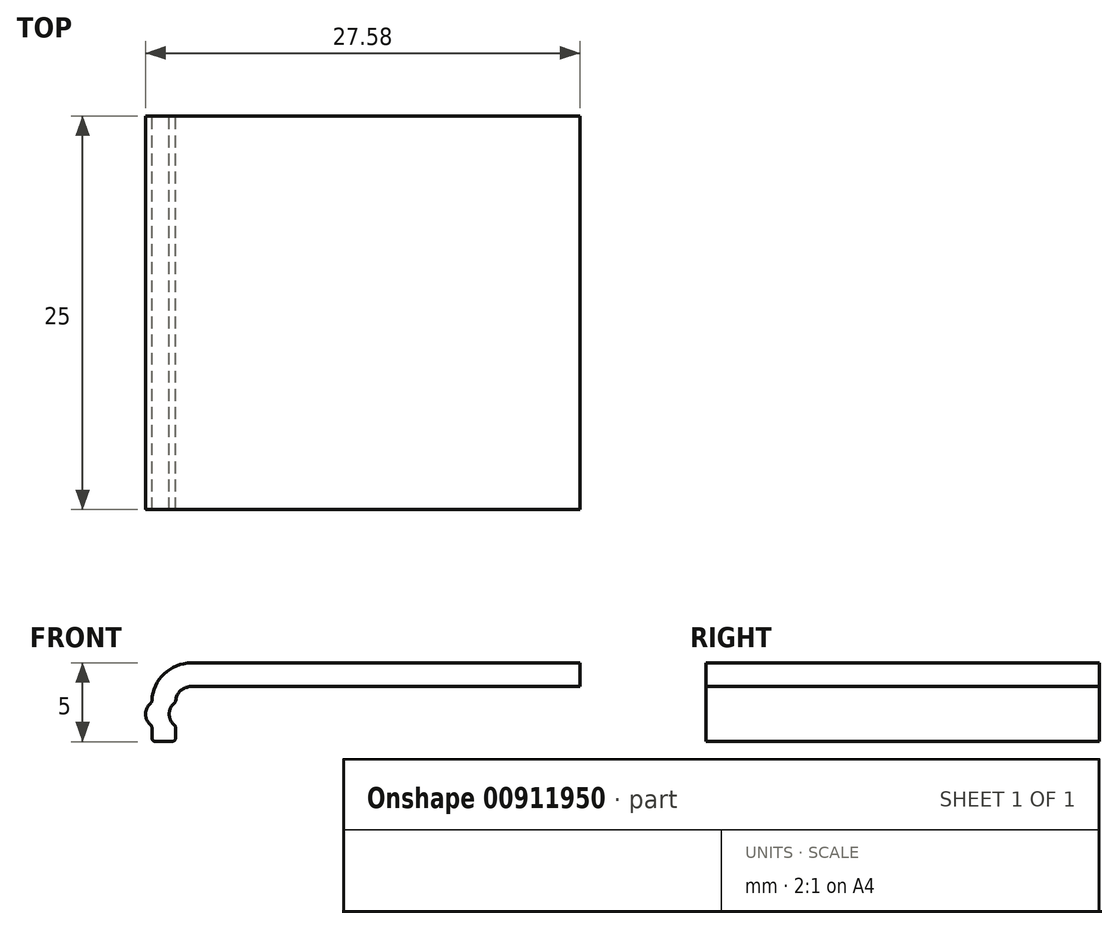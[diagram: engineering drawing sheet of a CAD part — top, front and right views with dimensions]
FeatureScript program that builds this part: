
annotation { "Feature Type Name" : "Feature", "Feature Type Description" : "" }
export const myFeature = defineFeature(function(context is Context, id is Id, definition is map)
    precondition{}
    {
        {
            var Q0;
            Q0=qCreatedBy(makeId("Front.planeOp"),FACE);
            var sketch = newSketch(context, id + "F0", { "sketchPlane" : qUnion([Q0])});
            skLineSegment(sketch, "E0", {"start": v(0, 0) * mm, "end": v(-24.68, 0) * mm});
            skArc(sketch, "E1", {"start": v(-24.68, 0) * mm, "mid": v(-25.4, -0.3) * mm, "end": v(-25.68, -1) * mm});
            skLineSegment(sketch, "E2", {"start": v(-25.68, -1) * mm, "end": v(-25.68, -1) * mm});
            skArc(sketch, "E3", {"start": v(-25.68, -1) * mm, "mid": v(-26.08, -1.75) * mm, "end": v(-25.68, -2.5) * mm});
            skLineSegment(sketch, "E4", {"start": v(-25.68, -2.5) * mm, "end": v(-25.68, -3.5) * mm});
            skLineSegment(sketch, "E5", {"start": v(-27.18, -3.5) * mm, "end": v(-25.68, -3.5) * mm});
            skLineSegment(sketch, "E6", {"start": v(-25.68, -1) * mm, "end": v(-25.68, -2.5) * mm, "construction": true});
            skLineSegment(sketch, "E7", {"start": v(-25.68, -1.75) * mm, "end": v(-26.08, -1.75) * mm, "construction": true});
            skLineSegment(sketch, "E8", {"start": v(-27.18, -3.5) * mm, "end": v(-27.18, -2.5) * mm});
            skArc(sketch, "E9", {"start": v(-27.18, -1) * mm, "mid": v(-27.58, -1.75) * mm, "end": v(-27.18, -2.5) * mm});
            skLineSegment(sketch, "E10", {"start": v(-27.18, -1) * mm, "end": v(-27.18, -1) * mm});
            skLineSegment(sketch, "E11", {"start": v(-27.18, -1) * mm, "end": v(-27.18, -2.5) * mm, "construction": true});
            skLineSegment(sketch, "E12", {"start": v(-27.18, -1.75) * mm, "end": v(-27.58, -1.75) * mm, "construction": true});
            skArc(sketch, "E13", {"start": v(-24.68, 1.5) * mm, "mid": v(-26.45, 0.77) * mm, "end": v(-27.18, -1) * mm});
            skLineSegment(sketch, "E14", {"start": v(-24.68, 1.5) * mm, "end": v(0, 1.5) * mm});
            skLineSegment(sketch, "E15", {"start": v(0, 1.5) * mm, "end": v(0, 0) * mm});
            skSolve(sketch);
        }
        {
            var Q0;
            Q0=makeQuery(id+"F0.imprint","IMPRINT",FACE,{"disambiguationData":[TD([[makeQuery(id+"F0.imprint","IMPRINT",EDGE,{"derivedFrom":sQuery(id+"F0.wireOp",EDGE,"E0")}),-1.0]])]});
            extrude(context, id + "F1", {"entities" : qUnion([Q0]), "depth" : 25 * mm, "offsetDistance" : 25 * mm});
        }
        {
            var Q0;
            Q0=makeQuery(id+"F1.opExtrude","SWEPT_EDGE",EDGE,{"disambiguationData":[OSD([sQuery(id+"F0.wireOp",EDGE,"E5"),sQuery(id+"F0.wireOp",EDGE,"E8")])]});
            var Q1;
            Q1=makeQuery(id+"F1.opExtrude","SWEPT_EDGE",EDGE,{"disambiguationData":[OSD([sQuery(id+"F0.wireOp",EDGE,"E4"),sQuery(id+"F0.wireOp",EDGE,"E5")])]});
            var Q2;
            Q2=makeQuery(id+"F1.opExtrude","SWEPT_EDGE",EDGE,{"disambiguationData":[OSD([sQuery(id+"F0.wireOp",EDGE,"E3"),sQuery(id+"F0.wireOp",EDGE,"E4")])]});
            var Q3;
            Q3=makeQuery(id+"F1.opExtrude","SWEPT_EDGE",EDGE,{"disambiguationData":[OSD([sQuery(id+"F0.wireOp",EDGE,"E1"),sQuery(id+"F0.wireOp",EDGE,"E3")])]});
            var Q4;
            Q4=makeQuery(id+"F1.opExtrude","SWEPT_EDGE",EDGE,{"disambiguationData":[OSD([sQuery(id+"F0.wireOp",EDGE,"E9"),sQuery(id+"F0.wireOp",EDGE,"E10")])]});
            var Q5;
            Q5=makeQuery(id+"F1.opExtrude","SWEPT_EDGE",EDGE,{"disambiguationData":[OSD([sQuery(id+"F0.wireOp",EDGE,"E8"),sQuery(id+"F0.wireOp",EDGE,"E9")])]});
            fillet(context, id + "F2", {"entities" : qUnion([Q0, Q1, Q2, Q3, Q4, Q5]), "radius" : .25 * mm, "tangentPropagation" : true, "allowEdgeOverflow" : false});
        }
    });
